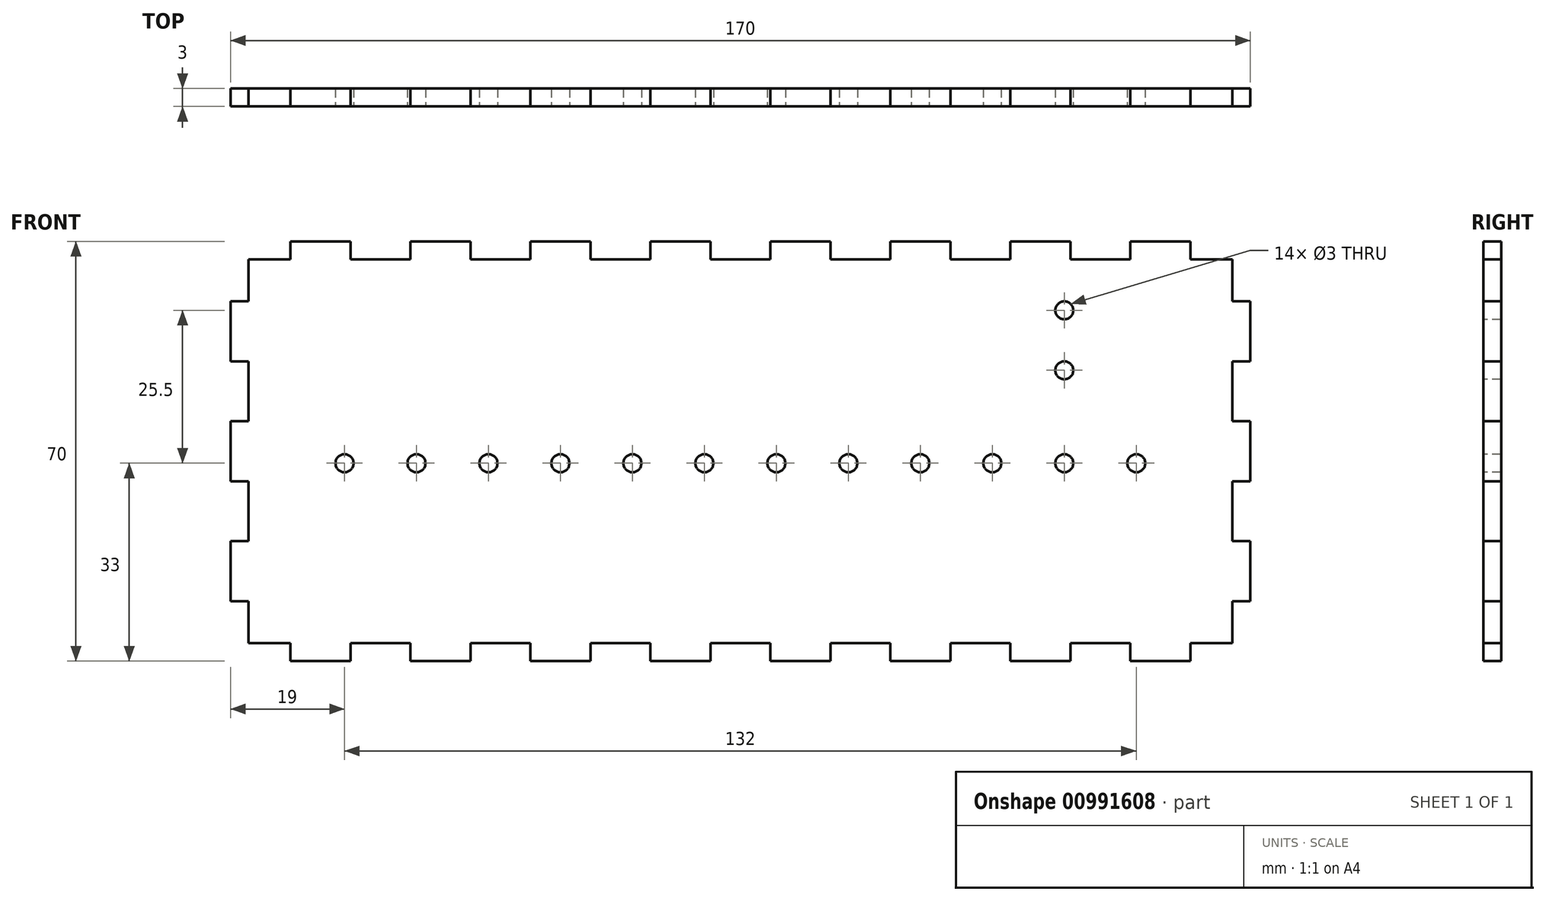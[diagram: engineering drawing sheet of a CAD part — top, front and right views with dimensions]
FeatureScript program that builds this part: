
annotation { "Feature Type Name" : "Feature", "Feature Type Description" : "" }
export const myFeature = defineFeature(function(context is Context, id is Id, definition is map)
    precondition{}
    {
        {
            var Q0;
            Q0=qCreatedBy(makeId("Front.planeOp"),FACE);
            var sketch = newSketch(context, id + "F0", { "sketchPlane" : qUnion([Q0])});
            skLineSegment(sketch, "E0.bottom", {"start": v(85, -35) * mm, "end": v(-85, -35) * mm});
            skLineSegment(sketch, "E0.top", {"start": v(85, 35) * mm, "end": v(-85, 35) * mm});
            skLineSegment(sketch, "E0.left", {"start": v(85, -35) * mm, "end": v(85, 35) * mm});
            skLineSegment(sketch, "E0.right", {"start": v(-85, -35) * mm, "end": v(-85, 35) * mm});
            skPoint(sketch, "E0.middle", {"position": v(0, 0) * mm});
            skSolve(sketch);
        }
        {
            var Q0;
            Q0=makeQuery(id+"F0.imprint","IMPRINT",FACE,{"disambiguationData":[TD([[makeQuery(id+"F0.imprint","IMPRINT",EDGE,{"derivedFrom":sQuery(id+"F0.wireOp",EDGE,"E0.bottom")}),-1.0]])]});
            extrude(context, id + "F1", {"entities" : qUnion([Q0]), "depth" : 3 * mm, "offsetDistance" : 25 * mm});
        }
        {
            var Q0;
            Q0=makeQuery(id+"F1.opExtrude","CAP_FACE",FACE,{"disambiguationData":[OSD([sQuery(id+"F0.wireOp",EDGE,"E0.bottom"),sQuery(id+"F0.wireOp",EDGE,"E0.top"),sQuery(id+"F0.wireOp",EDGE,"E0.left"),sQuery(id+"F0.wireOp",EDGE,"E0.right")])],"isStart":false});
            var sketch = newSketch(context, id + "F2", { "sketchPlane" : qUnion([Q0])});
            skLineSegment(sketch, "E1", {"start": v(-85, -2) * mm, "end": v(85, -2) * mm, "construction": true});
            skLineSegment(sketch, "E2", {"start": v(-66, -15) * mm, "end": v(-66, -2) * mm, "construction": true});
            skCircle(sketch, "E3", {"center": v(-66, -2) * mm, "radius": 1.5 * mm});
            skCircle(sketch, "E4.1.0.0", {"center": v(-54, -2) * mm, "radius": 1.5 * mm});
            skCircle(sketch, "E4.2.0.0", {"center": v(-42, -2) * mm, "radius": 1.5 * mm});
            skCircle(sketch, "E4.3.0.0", {"center": v(-30, -2) * mm, "radius": 1.5 * mm});
            skCircle(sketch, "E4.4.0.0", {"center": v(-18, -2) * mm, "radius": 1.5 * mm});
            skCircle(sketch, "E4.5.0.0", {"center": v(-6, -2) * mm, "radius": 1.5 * mm});
            skCircle(sketch, "E4.6.0.0", {"center": v(6, -2) * mm, "radius": 1.5 * mm});
            skCircle(sketch, "E4.7.0.0", {"center": v(18, -2) * mm, "radius": 1.5 * mm});
            skCircle(sketch, "E4.8.0.0", {"center": v(30, -2) * mm, "radius": 1.5 * mm});
            skCircle(sketch, "E4.9.0.0", {"center": v(42, -2) * mm, "radius": 1.5 * mm});
            skCircle(sketch, "E4.10.0.0", {"center": v(54, -2) * mm, "radius": 1.5 * mm});
            skCircle(sketch, "E4.11.0.0", {"center": v(66, -2) * mm, "radius": 1.5 * mm});
            skLineSegment(sketch, "E4.direction1", {"start": v(-66, -2) * mm, "end": v(-54, -2) * mm, "construction": true});
            skSolve(sketch);
        }
        {
            var Q0;
            Q0=qSketchRegion(id+"F2",true);
            extrude(context, id + "F3", {"entities" : qUnion([Q0]), "operationType" : NewBodyOperationType.REMOVE, "endBound" : BoundingType.THROUGH_ALL, "oppositeDirection" : true, "depth" : 25 * mm, "offsetDistance" : 25 * mm});
        }
        {
            var Q0;
            Q0=makeQuery(id+"F1.opExtrude","CAP_FACE",FACE,{"disambiguationData":[OSD([sQuery(id+"F0.wireOp",EDGE,"E0.bottom"),sQuery(id+"F0.wireOp",EDGE,"E0.top"),sQuery(id+"F0.wireOp",EDGE,"E0.left"),sQuery(id+"F0.wireOp",EDGE,"E0.right")])],"isStart":false});
            var sketch = newSketch(context, id + "F4", { "sketchPlane" : qUnion([Q0])});
            skLineSegment(sketch, "E5", {"start": v(54, -2) * mm, "end": v(54, 8.14) * mm, "construction": true});
            skCircle(sketch, "E6", {"center": v(54, 13.5) * mm, "radius": 1.5 * mm});
            skCircle(sketch, "E7.0.1.0", {"center": v(54, 23.5) * mm, "radius": 1.5 * mm});
            skLineSegment(sketch, "E7.direction1", {"start": v(54, 13.5) * mm, "end": v(79, 13.5) * mm, "construction": true});
            skLineSegment(sketch, "E7.direction2", {"start": v(54, 13.5) * mm, "end": v(54, 23.5) * mm, "construction": true});
            skSolve(sketch);
        }
        {
            var Q0;
            Q0=qSketchRegion(id+"F4",true);
            extrude(context, id + "F5", {"entities" : qUnion([Q0]), "operationType" : NewBodyOperationType.REMOVE, "endBound" : BoundingType.THROUGH_ALL, "oppositeDirection" : true, "depth" : 25 * mm, "offsetDistance" : 25 * mm});
        }
        {
            var Q0;
            Q0=makeQuery(id+"F1.opExtrude","CAP_FACE",FACE,{"disambiguationData":[OSD([sQuery(id+"F0.wireOp",EDGE,"E0.bottom"),sQuery(id+"F0.wireOp",EDGE,"E0.top"),sQuery(id+"F0.wireOp",EDGE,"E0.left"),sQuery(id+"F0.wireOp",EDGE,"E0.right")])],"isStart":false});
            var sketch = newSketch(context, id + "F6", { "sketchPlane" : qUnion([Q0])});
            skLineSegment(sketch, "E8.bottom", {"start": v(-85, -35) * mm, "end": v(-75, -35) * mm});
            skLineSegment(sketch, "E8.top", {"start": v(-85, -32) * mm, "end": v(-75, -32) * mm});
            skLineSegment(sketch, "E8.left", {"start": v(-85, -35) * mm, "end": v(-85, -32) * mm});
            skLineSegment(sketch, "E8.right", {"start": v(-75, -35) * mm, "end": v(-75, -32) * mm});
            skLineSegment(sketch, "E9.1.0.0", {"start": v(-55, -35) * mm, "end": v(-55, -32) * mm});
            skLineSegment(sketch, "E9.1.0.1", {"start": v(-65, -35) * mm, "end": v(-65, -32) * mm});
            skLineSegment(sketch, "E9.1.0.2", {"start": v(-65, -35) * mm, "end": v(-55, -35) * mm});
            skLineSegment(sketch, "E9.1.0.3", {"start": v(-65, -32) * mm, "end": v(-55, -32) * mm});
            skLineSegment(sketch, "E9.2.0.0", {"start": v(-35, -35) * mm, "end": v(-35, -32) * mm});
            skLineSegment(sketch, "E9.2.0.1", {"start": v(-45, -35) * mm, "end": v(-45, -32) * mm});
            skLineSegment(sketch, "E9.2.0.2", {"start": v(-45, -35) * mm, "end": v(-35, -35) * mm});
            skLineSegment(sketch, "E9.2.0.3", {"start": v(-45, -32) * mm, "end": v(-35, -32) * mm});
            skLineSegment(sketch, "E9.3.0.0", {"start": v(-15, -35) * mm, "end": v(-15, -32) * mm});
            skLineSegment(sketch, "E9.3.0.1", {"start": v(-25, -35) * mm, "end": v(-25, -32) * mm});
            skLineSegment(sketch, "E9.3.0.2", {"start": v(-25, -35) * mm, "end": v(-15, -35) * mm});
            skLineSegment(sketch, "E9.3.0.3", {"start": v(-25, -32) * mm, "end": v(-15, -32) * mm});
            skLineSegment(sketch, "E9.4.0.0", {"start": v(5, -35) * mm, "end": v(5, -32) * mm});
            skLineSegment(sketch, "E9.4.0.1", {"start": v(-5, -35) * mm, "end": v(-5, -32) * mm});
            skLineSegment(sketch, "E9.4.0.2", {"start": v(-5, -35) * mm, "end": v(5, -35) * mm});
            skLineSegment(sketch, "E9.4.0.3", {"start": v(-5, -32) * mm, "end": v(5, -32) * mm});
            skLineSegment(sketch, "E9.5.0.0", {"start": v(25, -35) * mm, "end": v(25, -32) * mm});
            skLineSegment(sketch, "E9.5.0.1", {"start": v(15, -35) * mm, "end": v(15, -32) * mm});
            skLineSegment(sketch, "E9.5.0.2", {"start": v(15, -35) * mm, "end": v(25, -35) * mm});
            skLineSegment(sketch, "E9.5.0.3", {"start": v(15, -32) * mm, "end": v(25, -32) * mm});
            skLineSegment(sketch, "E9.6.0.0", {"start": v(45, -35) * mm, "end": v(45, -32) * mm});
            skLineSegment(sketch, "E9.6.0.1", {"start": v(35, -35) * mm, "end": v(35, -32) * mm});
            skLineSegment(sketch, "E9.6.0.2", {"start": v(35, -35) * mm, "end": v(45, -35) * mm});
            skLineSegment(sketch, "E9.6.0.3", {"start": v(35, -32) * mm, "end": v(45, -32) * mm});
            skLineSegment(sketch, "E9.7.0.0", {"start": v(65, -35) * mm, "end": v(65, -32) * mm});
            skLineSegment(sketch, "E9.7.0.1", {"start": v(55, -35) * mm, "end": v(55, -32) * mm});
            skLineSegment(sketch, "E9.7.0.2", {"start": v(55, -35) * mm, "end": v(65, -35) * mm});
            skLineSegment(sketch, "E9.7.0.3", {"start": v(55, -32) * mm, "end": v(65, -32) * mm});
            skLineSegment(sketch, "E9.8.0.0", {"start": v(85, -35) * mm, "end": v(85, -32) * mm});
            skLineSegment(sketch, "E9.8.0.1", {"start": v(75, -35) * mm, "end": v(75, -32) * mm});
            skLineSegment(sketch, "E9.8.0.2", {"start": v(75, -35) * mm, "end": v(85, -35) * mm});
            skLineSegment(sketch, "E9.8.0.3", {"start": v(75, -32) * mm, "end": v(85, -32) * mm});
            skLineSegment(sketch, "E9.direction1", {"start": v(-85, -35) * mm, "end": v(-65, -35) * mm, "construction": true});
            skLineSegment(sketch, "E10", {"start": v(-85, 0) * mm, "end": v(85, 0) * mm, "construction": true});
            skLineSegment(sketch, "E11.MirrorCS", {"start": v(-65, 35) * mm, "end": v(-65, 32) * mm});
            skLineSegment(sketch, "E12.MirrorCS", {"start": v(-25, 35) * mm, "end": v(-25, 32) * mm});
            skLineSegment(sketch, "E13.MirrorCS", {"start": v(-35, 35) * mm, "end": v(-35, 32) * mm});
            skLineSegment(sketch, "E14.MirrorCS", {"start": v(-5, 35) * mm, "end": v(-5, 32) * mm});
            skLineSegment(sketch, "E15.MirrorCS", {"start": v(-85, 35) * mm, "end": v(-85, 32) * mm});
            skLineSegment(sketch, "E16.MirrorCS", {"start": v(75, 35) * mm, "end": v(75, 32) * mm});
            skLineSegment(sketch, "E17.MirrorCS", {"start": v(25, 35) * mm, "end": v(25, 32) * mm});
            skLineSegment(sketch, "E18.MirrorCS", {"start": v(-45, 35) * mm, "end": v(-45, 32) * mm});
            skLineSegment(sketch, "E19.MirrorCS", {"start": v(45, 35) * mm, "end": v(45, 32) * mm});
            skLineSegment(sketch, "E20.MirrorCS", {"start": v(-55, 35) * mm, "end": v(-55, 32) * mm});
            skLineSegment(sketch, "E21.MirrorCS", {"start": v(85, 35) * mm, "end": v(85, 32) * mm});
            skLineSegment(sketch, "E22.MirrorCS", {"start": v(-15, 35) * mm, "end": v(-15, 32) * mm});
            skLineSegment(sketch, "E23.MirrorCS", {"start": v(55, 35) * mm, "end": v(55, 32) * mm});
            skLineSegment(sketch, "E24.MirrorCS", {"start": v(65, 35) * mm, "end": v(65, 32) * mm});
            skLineSegment(sketch, "E25.MirrorCS", {"start": v(15, 35) * mm, "end": v(15, 32) * mm});
            skLineSegment(sketch, "E26.MirrorCS", {"start": v(35, 35) * mm, "end": v(35, 32) * mm});
            skLineSegment(sketch, "E27.MirrorCS", {"start": v(5, 35) * mm, "end": v(5, 32) * mm});
            skLineSegment(sketch, "E28.MirrorCS", {"start": v(-75, 35) * mm, "end": v(-75, 32) * mm});
            skLineSegment(sketch, "E29.MirrorCS", {"start": v(-85, 35) * mm, "end": v(-75, 35) * mm});
            skLineSegment(sketch, "E30.MirrorCS", {"start": v(-25, 35) * mm, "end": v(-15, 35) * mm});
            skLineSegment(sketch, "E31.MirrorCS", {"start": v(55, 35) * mm, "end": v(65, 35) * mm});
            skLineSegment(sketch, "E32.MirrorCS", {"start": v(-25, 32) * mm, "end": v(-15, 32) * mm});
            skLineSegment(sketch, "E33.MirrorCS", {"start": v(35, 32) * mm, "end": v(45, 32) * mm});
            skLineSegment(sketch, "E34.MirrorCS", {"start": v(55, 32) * mm, "end": v(65, 32) * mm});
            skLineSegment(sketch, "E35.MirrorCS", {"start": v(15, 35) * mm, "end": v(25, 35) * mm});
            skLineSegment(sketch, "E36.MirrorCS", {"start": v(-65, 32) * mm, "end": v(-55, 32) * mm});
            skLineSegment(sketch, "E37.MirrorCS", {"start": v(35, 35) * mm, "end": v(45, 35) * mm});
            skLineSegment(sketch, "E38.MirrorCS", {"start": v(-45, 35) * mm, "end": v(-35, 35) * mm});
            skLineSegment(sketch, "E39.MirrorCS", {"start": v(75, 32) * mm, "end": v(85, 32) * mm});
            skLineSegment(sketch, "E40.MirrorCS", {"start": v(-5, 32) * mm, "end": v(5, 32) * mm});
            skLineSegment(sketch, "E41.MirrorCS", {"start": v(-65, 35) * mm, "end": v(-55, 35) * mm});
            skLineSegment(sketch, "E42.MirrorCS", {"start": v(-85, 35) * mm, "end": v(-65, 35) * mm, "construction": true});
            skLineSegment(sketch, "E43.MirrorCS", {"start": v(-45, 32) * mm, "end": v(-35, 32) * mm});
            skLineSegment(sketch, "E44.MirrorCS", {"start": v(-5, 35) * mm, "end": v(5, 35) * mm});
            skLineSegment(sketch, "E45.MirrorCS", {"start": v(-85, 32) * mm, "end": v(-75, 32) * mm});
            skLineSegment(sketch, "E46.MirrorCS", {"start": v(75, 35) * mm, "end": v(85, 35) * mm});
            skLineSegment(sketch, "E47.MirrorCS", {"start": v(15, 32) * mm, "end": v(25, 32) * mm});
            skLineSegment(sketch, "E48.bottom", {"start": v(-85, 35) * mm, "end": v(-82, 35) * mm});
            skLineSegment(sketch, "E48.top", {"start": v(-85, 25) * mm, "end": v(-82, 25) * mm});
            skLineSegment(sketch, "E48.left", {"start": v(-85, 35) * mm, "end": v(-85, 25) * mm});
            skLineSegment(sketch, "E48.right", {"start": v(-82, 35) * mm, "end": v(-82, 25) * mm});
            skLineSegment(sketch, "E49.0.1.0", {"start": v(-82, 15) * mm, "end": v(-82, 5) * mm});
            skLineSegment(sketch, "E49.0.1.1", {"start": v(-85, 15) * mm, "end": v(-85, 5) * mm});
            skLineSegment(sketch, "E49.0.1.2", {"start": v(-85, 5) * mm, "end": v(-82, 5) * mm});
            skLineSegment(sketch, "E49.0.1.3", {"start": v(-85, 15) * mm, "end": v(-82, 15) * mm});
            skLineSegment(sketch, "E49.0.1.4", {"start": v(-85, 15) * mm, "end": v(-85, 12) * mm});
            skLineSegment(sketch, "E49.0.2.0", {"start": v(-82, -5) * mm, "end": v(-82, -15) * mm});
            skLineSegment(sketch, "E49.0.2.1", {"start": v(-85, -5) * mm, "end": v(-85, -15) * mm});
            skLineSegment(sketch, "E49.0.2.2", {"start": v(-85, -15) * mm, "end": v(-82, -15) * mm});
            skLineSegment(sketch, "E49.0.2.3", {"start": v(-85, -5) * mm, "end": v(-82, -5) * mm});
            skLineSegment(sketch, "E49.0.2.4", {"start": v(-85, -5) * mm, "end": v(-85, -8) * mm});
            skLineSegment(sketch, "E49.0.3.0", {"start": v(-82, -25) * mm, "end": v(-82, -35) * mm});
            skLineSegment(sketch, "E49.0.3.1", {"start": v(-85, -25) * mm, "end": v(-85, -35) * mm});
            skLineSegment(sketch, "E49.0.3.2", {"start": v(-85, -35) * mm, "end": v(-82, -35) * mm});
            skLineSegment(sketch, "E49.0.3.3", {"start": v(-85, -25) * mm, "end": v(-82, -25) * mm});
            skLineSegment(sketch, "E49.0.3.4", {"start": v(-85, -25) * mm, "end": v(-85, -28) * mm});
            skLineSegment(sketch, "E49.direction1", {"start": v(-85, 25) * mm, "end": v(-60, 25) * mm, "construction": true});
            skLineSegment(sketch, "E49.direction2", {"start": v(-85, 25) * mm, "end": v(-85, 5) * mm, "construction": true});
            skLineSegment(sketch, "E50", {"start": v(0, 35) * mm, "end": v(0, -35) * mm, "construction": true});
            skLineSegment(sketch, "E51.MirrorCS", {"start": v(85, -25) * mm, "end": v(85, -28) * mm});
            skLineSegment(sketch, "E52.MirrorCS", {"start": v(85, 15) * mm, "end": v(85, 12) * mm});
            skLineSegment(sketch, "E53.MirrorCS", {"start": v(85, -5) * mm, "end": v(85, -8) * mm});
            skLineSegment(sketch, "E54.MirrorCS", {"start": v(85, 15) * mm, "end": v(85, 5) * mm});
            skLineSegment(sketch, "E55.MirrorCS", {"start": v(85, 5) * mm, "end": v(82, 5) * mm});
            skLineSegment(sketch, "E56.MirrorCS", {"start": v(82, 15) * mm, "end": v(82, 5) * mm});
            skLineSegment(sketch, "E57.MirrorCS", {"start": v(85, -35) * mm, "end": v(82, -35) * mm});
            skLineSegment(sketch, "E58.MirrorCS", {"start": v(85, -5) * mm, "end": v(85, -15) * mm});
            skLineSegment(sketch, "E59.MirrorCS", {"start": v(85, 35) * mm, "end": v(82, 35) * mm});
            skLineSegment(sketch, "E60.MirrorCS", {"start": v(85, 25) * mm, "end": v(85, 5) * mm, "construction": true});
            skLineSegment(sketch, "E61.MirrorCS", {"start": v(82, -25) * mm, "end": v(82, -35) * mm});
            skLineSegment(sketch, "E62.MirrorCS", {"start": v(85, 15) * mm, "end": v(82, 15) * mm});
            skLineSegment(sketch, "E63.MirrorCS", {"start": v(85, -15) * mm, "end": v(82, -15) * mm});
            skLineSegment(sketch, "E64.MirrorCS", {"start": v(85, -25) * mm, "end": v(82, -25) * mm});
            skLineSegment(sketch, "E65.MirrorCS", {"start": v(85, 25) * mm, "end": v(82, 25) * mm});
            skLineSegment(sketch, "E66.MirrorCS", {"start": v(82, 35) * mm, "end": v(82, 25) * mm});
            skLineSegment(sketch, "E67.MirrorCS", {"start": v(85, 35) * mm, "end": v(85, 25) * mm});
            skLineSegment(sketch, "E68.MirrorCS", {"start": v(85, -25) * mm, "end": v(85, -35) * mm});
            skLineSegment(sketch, "E69.MirrorCS", {"start": v(85, -5) * mm, "end": v(82, -5) * mm});
            skLineSegment(sketch, "E70.MirrorCS", {"start": v(82, -5) * mm, "end": v(82, -15) * mm});
            skSolve(sketch);
        }
        {
            var Q0;
            Q0=qSketchRegion(id+"F6",true);
            extrude(context, id + "F7", {"entities" : qUnion([Q0]), "operationType" : NewBodyOperationType.REMOVE, "endBound" : BoundingType.THROUGH_ALL, "oppositeDirection" : true, "depth" : 25 * mm, "offsetDistance" : 25 * mm});
        }
    });
